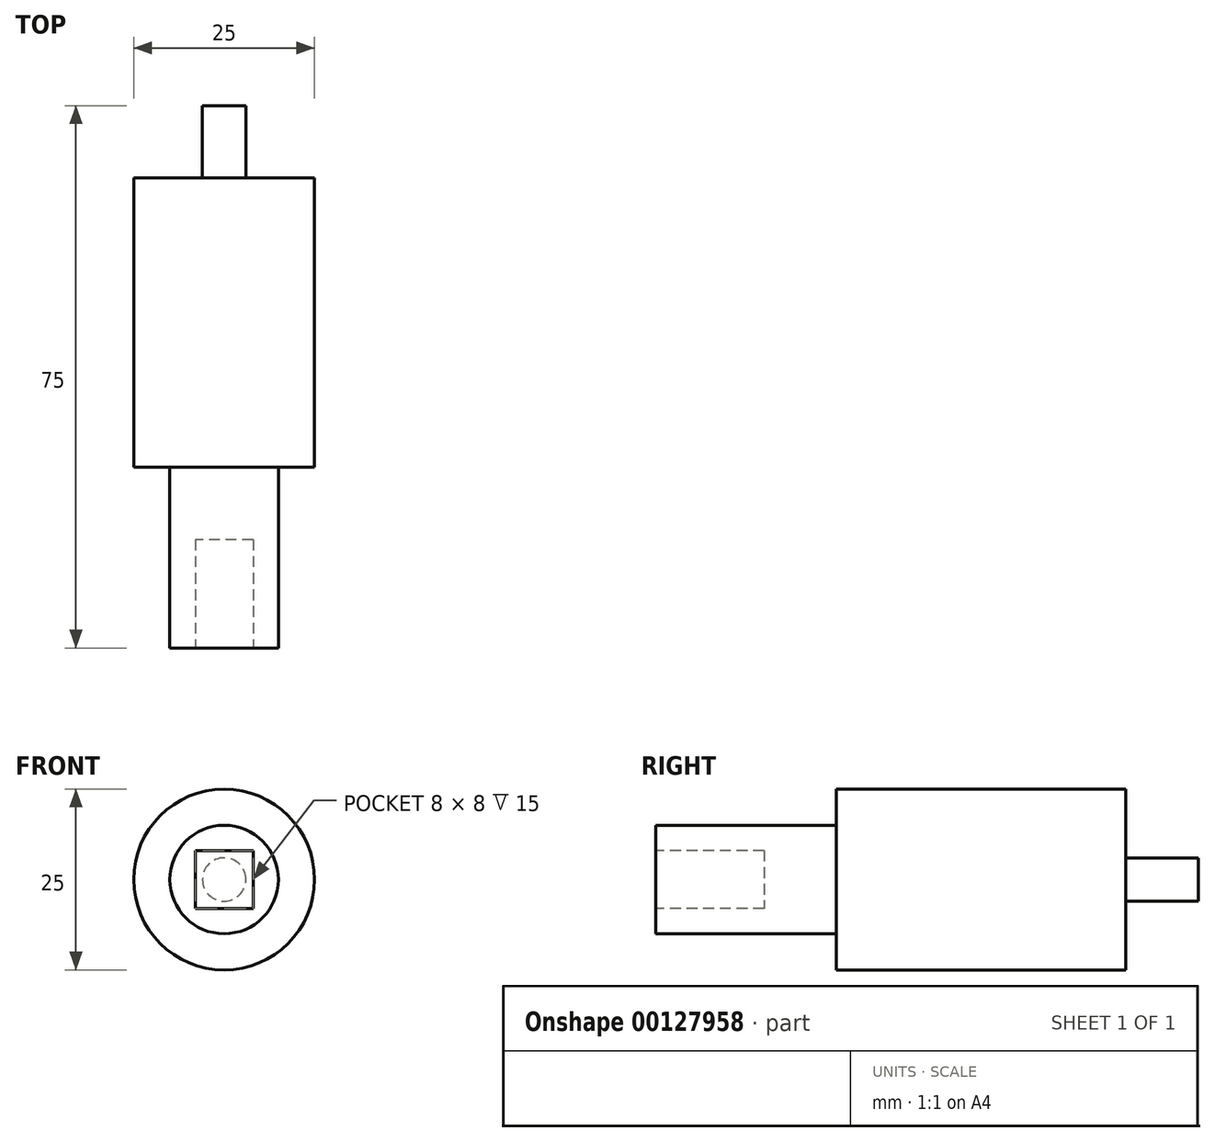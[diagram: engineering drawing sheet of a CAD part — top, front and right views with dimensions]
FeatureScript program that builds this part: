
annotation { "Feature Type Name" : "Feature", "Feature Type Description" : "" }
export const myFeature = defineFeature(function(context is Context, id is Id, definition is map)
    precondition{}
    {
        {
            var Q0;
            Q0=qCreatedBy(makeId("Front.planeOp"),FACE);
            var sketch = newSketch(context, id + "F0", { "sketchPlane" : qUnion([Q0])});
            skCircle(sketch, "E0", {"center": v(0, 0) * mm, "radius": 3 * mm});
            skSolve(sketch);
        }
        {
            var Q0;
            Q0=makeQuery(id+"F0.imprint","IMPRINT",FACE,{"disambiguationData":[TD([[makeQuery(id+"F0.imprint","IMPRINT",EDGE,{"derivedFrom":sQuery(id+"F0.wireOp",EDGE,"E0")}),1.0]])]});
            extrude(context, id + "F1", {"entities" : qUnion([Q0]), "depth" : 10 * mm});
        }
        {
            var Q0;
            Q0=makeQuery(id+"F1.opExtrude","CAP_FACE",FACE,{"disambiguationData":[OSD([sQuery(id+"F0.wireOp",EDGE,"E0")])],"isStart":false});
            var sketch = newSketch(context, id + "F2", { "sketchPlane" : qUnion([Q0])});
            skCircle(sketch, "E1", {"center": v(0, 0) * mm, "radius": 12.5 * mm});
            skSolve(sketch);
        }
        {
            var Q0;
            Q0=makeQuery(id+"F2.imprint","IMPRINT",FACE,{"disambiguationData":[TD([[makeQuery(id+"F2.imprint","IMPRINT",EDGE,{"derivedFrom":sQuery(id+"F2.wireOp",EDGE,"E1")}),1.0]])]});
            var Q1;
            Q1=makeQuery(id+"F2.imprint","IMPRINT",FACE,{"disambiguationData":[TD([[makeQuery(id+"F2.imprint","IMPRINT",EDGE,{"derivedFrom":makeQuery(id+"F1.opExtrude","CAP_EDGE",EDGE,{"disambiguationData":[OSD([sQuery(id+"F0.wireOp",EDGE,"E0")])],"isStart":false})}),1.0]])]});
            extrude(context, id + "F3", {"entities" : qUnion([Q0, Q1]), "operationType" : NewBodyOperationType.ADD, "depth" : 40 * mm});
        }
        {
            var Q0;
            Q0=makeQuery(id+"F3.opExtrude","CAP_FACE",FACE,{"disambiguationData":[OSD([sQuery(id+"F2.wireOp",EDGE,"E1")])],"isStart":false});
            var sketch = newSketch(context, id + "F4", { "sketchPlane" : qUnion([Q0])});
            skCircle(sketch, "E2", {"center": v(0, 0) * mm, "radius": 7.5 * mm});
            skSolve(sketch);
        }
        {
            var Q0;
            Q0=makeQuery(id+"F4.imprint","IMPRINT",FACE,{"disambiguationData":[TD([[makeQuery(id+"F4.imprint","IMPRINT",EDGE,{"derivedFrom":sQuery(id+"F4.wireOp",EDGE,"E2")}),1.0]])]});
            extrude(context, id + "F5", {"entities" : qUnion([Q0]), "operationType" : NewBodyOperationType.ADD, "depth" : 25 * mm});
        }
        {
            var Q0;
            Q0=makeQuery(id+"F5.opExtrude","CAP_FACE",FACE,{"disambiguationData":[OSD([sQuery(id+"F4.wireOp",EDGE,"E2")])],"isStart":false});
            var sketch = newSketch(context, id + "F6", { "sketchPlane" : qUnion([Q0])});
            skLineSegment(sketch, "E3.bottom", {"start": v(4, 4) * mm, "end": v(-4, 4) * mm});
            skLineSegment(sketch, "E3.top", {"start": v(4, -4) * mm, "end": v(-4, -4) * mm});
            skLineSegment(sketch, "E3.left", {"start": v(4, 4) * mm, "end": v(4, -4) * mm});
            skLineSegment(sketch, "E3.right", {"start": v(-4, 4) * mm, "end": v(-4, -4) * mm});
            skPoint(sketch, "E3.middle", {"position": v(0, 0) * mm});
            skSolve(sketch);
        }
        {
            var Q0;
            Q0=makeQuery(id+"F6.imprint","IMPRINT",FACE,{"disambiguationData":[TD([[makeQuery(id+"F6.imprint","IMPRINT",EDGE,{"derivedFrom":sQuery(id+"F6.wireOp",EDGE,"E3.bottom")}),1.0]])]});
            extrude(context, id + "F7", {"entities" : qUnion([Q0]), "operationType" : NewBodyOperationType.REMOVE, "oppositeDirection" : true, "depth" : 15 * mm});
        }
    });
